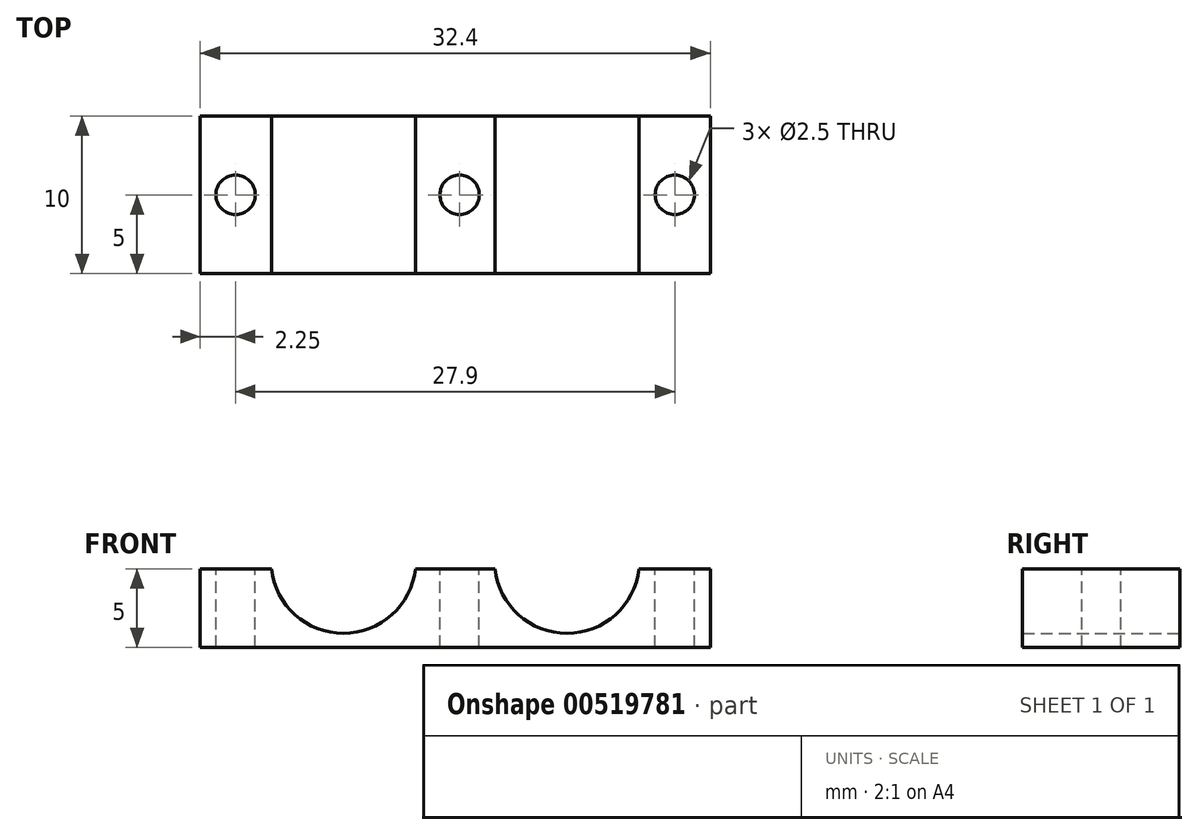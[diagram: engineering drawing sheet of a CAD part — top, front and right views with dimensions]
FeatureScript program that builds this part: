
annotation { "Feature Type Name" : "Feature", "Feature Type Description" : "" }
export const myFeature = defineFeature(function(context is Context, id is Id, definition is map)
    precondition{}
    {
        {
            var Q0;
            Q0=qCreatedBy(makeId("Front.planeOp"),FACE);
            var sketch = newSketch(context, id + "F0", { "sketchPlane" : qUnion([Q0])});
            skLineSegment(sketch, "E0.bottom", {"start": v(0, 5) * mm, "end": v(4.53, 5) * mm});
            skLineSegment(sketch, "E0.top", {"start": v(0, 0) * mm, "end": v(16.2, 0) * mm});
            skLineSegment(sketch, "E0.left", {"start": v(0, 5) * mm, "end": v(0, 0) * mm});
            skLineSegment(sketch, "E0.right", {"start": v(16.2, 5) * mm, "end": v(16.2, 0) * mm});
            skArc(sketch, "E1", {"start": v(4.53, 5) * mm, "mid": v(9.1, 0.9) * mm, "end": v(13.67, 5) * mm});
            skLineSegment(sketch, "E2.trimOffspring", {"start": v(13.67, 5) * mm, "end": v(16.2, 5) * mm});
            skSolve(sketch);
        }
        {
            var Q0;
            Q0=makeQuery(id+"F0.imprint","IMPRINT",FACE,{"disambiguationData":[TD([[makeQuery(id+"F0.imprint","IMPRINT",EDGE,{"derivedFrom":sQuery(id+"F0.wireOp",EDGE,"E0.bottom")}),-1.0]])]});
            extrude(context, id + "F1", {"entities" : qUnion([Q0]), "depth" : 10 * mm, "offsetDistance" : 25 * mm});
        }
        {
            var Q0;
            Q0=makeQuery(id+"F1.opExtrude","SWEPT_BODY",BODY,{"disambiguationData":[OSD([sQuery(id+"F0.wireOp",EDGE,"E0.bottom"),sQuery(id+"F0.wireOp",EDGE,"E0.top"),sQuery(id+"F0.wireOp",EDGE,"E0.left"),sQuery(id+"F0.wireOp",EDGE,"E0.right"),sQuery(id+"F0.wireOp",EDGE,"E1"),sQuery(id+"F0.wireOp",EDGE,"E2.trimOffspring")])]});
            var Q1;
            Q1=makeQuery(id+"F1.opExtrude","SWEPT_FACE",FACE,{"disambiguationData":[OSD([sQuery(id+"F0.wireOp",EDGE,"E0.right")])]});
            mirror(context, id + "F2", {"operationType" : NewBodyOperationType.ADD, "entities" : qUnion([Q0]), "mirrorPlane" : qUnion([Q1])});
        }
        {
            var Q0;
            {var subQ0=makeQuery(id+"F1.opExtrude","SWEPT_FACE",FACE,{"disambiguationData":[OSD([sQuery(id+"F0.wireOp",EDGE,"E2.trimOffspring")])]});Q0=makeQuery(id+"F2.boolean.opBoolean","MERGE",FACE,{"derivedFrom":[subQ0,makeQuery(id+"F2.opPattern","COPY",FACE,{"derivedFrom":subQ0,"instanceName":"1"})]});}
            var sketch = newSketch(context, id + "F3", { "sketchPlane" : qUnion([Q0])});
            skCircle(sketch, "E3", {"center": v(2.25, -5) * mm, "radius": 1.25 * mm});
            skCircle(sketch, "E4", {"center": v(16.48, -5) * mm, "radius": 1.25 * mm});
            skCircle(sketch, "E5", {"center": v(30.15, -5) * mm, "radius": 1.25 * mm});
            skSolve(sketch);
        }
        {
            var Q0;
            Q0 = qSketchRegion(id + "F3", true);
            extrude(context, id + "F4", {"entities" : qUnion([Q0]), "operationType" : NewBodyOperationType.REMOVE, "endBound" : BoundingType.THROUGH_ALL, "oppositeDirection" : true, "depth" : 25 * mm, "offsetDistance" : 25 * mm});
        }
    });
